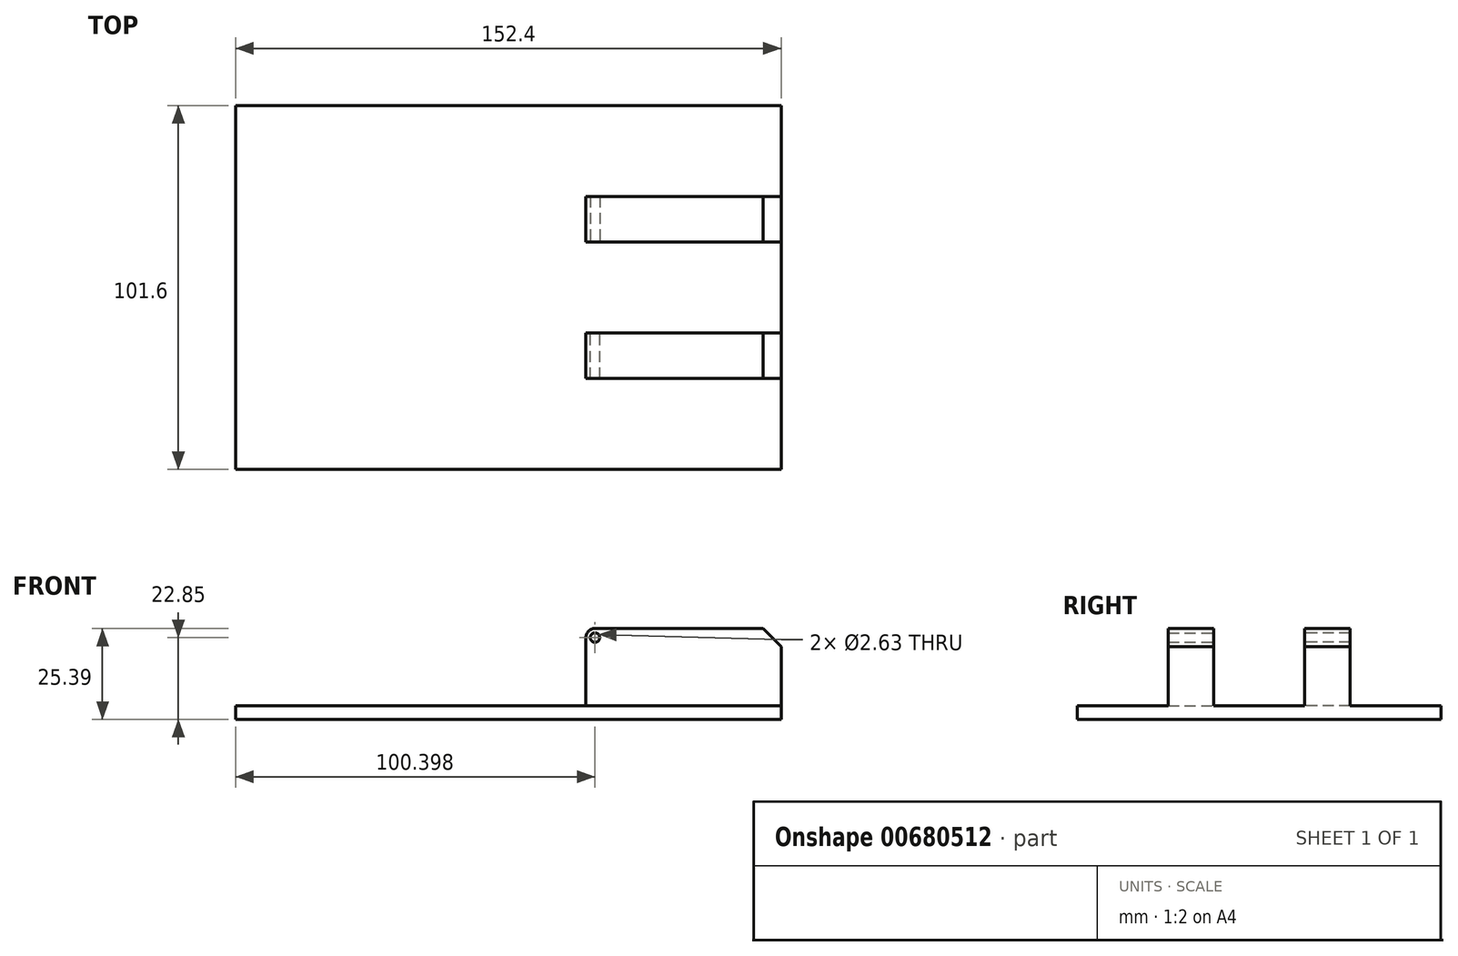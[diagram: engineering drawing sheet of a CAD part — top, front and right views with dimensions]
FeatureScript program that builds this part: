
annotation { "Feature Type Name" : "Feature", "Feature Type Description" : "" }
export const myFeature = defineFeature(function(context is Context, id is Id, definition is map)
    precondition{}
    {
        {
            var Q0;
            Q0=qCreatedBy(makeId("Front.planeOp"),FACE);
            var sketch = newSketch(context, id + "F0", { "sketchPlane" : qUnion([Q0])});
            skLineSegment(sketch, "E0.bottom", {"start": v(-7.2, 5.5) * mm, "end": v(145.2, 5.5) * mm});
            skLineSegment(sketch, "E0.top", {"start": v(-7.2, 1.7) * mm, "end": v(145.2, 1.7) * mm});
            skLineSegment(sketch, "E0.left", {"start": v(-7.2, 5.5) * mm, "end": v(-7.2, 1.7) * mm});
            skLineSegment(sketch, "E0.right", {"start": v(145.2, 5.5) * mm, "end": v(145.2, 1.7) * mm});
            skLineSegment(sketch, "E1.bottom", {"start": v(145.2, 5.5) * mm, "end": v(90.66, 5.5) * mm});
            skLineSegment(sketch, "E1.top", {"start": v(145.2, 27.08) * mm, "end": v(93.2, 27.08) * mm});
            skLineSegment(sketch, "E1.left", {"start": v(145.2, 5.5) * mm, "end": v(145.2, 27.08) * mm});
            skLineSegment(sketch, "E1.right", {"start": v(90.66, 5.5) * mm, "end": v(90.66, 24.54) * mm});
            skPoint(sketch, "E2.visualSharp", {"position": v(90.66, 27.08) * mm});
            skArc(sketch, "E2.filletArc", {"start": v(93.2, 27.08) * mm, "mid": v(91.4, 26.34) * mm, "end": v(90.66, 24.54) * mm});
            skCircle(sketch, "E3", {"center": v(93.2, 24.54) * mm, "radius": 1.31 * mm});
            skSolve(sketch);
        }
        {
            var Q0;
            Q0=makeQuery(id+"F0.imprint","IMPRINT",FACE,{"disambiguationData":[TD([[makeQuery(id+"F0.imprint","IMPRINT",EDGE,{"derivedFrom":sQuery(id+"F0.wireOp",EDGE,"E0.bottom")}),-1.0]])]});
            extrude(context, id + "F1", {"entities" : qUnion([Q0]), "endBound" : BoundingType.SYMMETRIC, "depth" : 101.6 * mm, "offsetDistance" : 25.4 * mm});
        }
        {
            var Q0;
            Q0 = qSketchRegion(id + "F0", true);
            extrude(context, id + "F2", {"entities" : qUnion([Q0]), "operationType" : NewBodyOperationType.ADD, "oppositeDirection" : true, "depth" : 25.4 * mm, "offsetDistance" : 25.4 * mm, "hasSecondDirection" : true, "secondDirectionOppositeDirection" : true, "secondDirectionDepth" : 12.7 * mm});
        }
        {
            var Q0;
            Q0 = qSketchRegion(id + "F0", true);
            extrude(context, id + "F3", {"entities" : qUnion([Q0]), "operationType" : NewBodyOperationType.ADD, "depth" : 25.4 * mm, "offsetDistance" : 25.4 * mm, "hasSecondDirection" : true, "secondDirectionOppositeDirection" : false, "secondDirectionDepth" : 12.7 * mm});
        }
        {
            var Q0;
            Q0=makeQuery(id+"F2.opExtrude","SWEPT_EDGE",EDGE,{"disambiguationData":[OSD([sQuery(id+"F0.wireOp",EDGE,"E1.top"),sQuery(id+"F0.wireOp",EDGE,"E1.left")])]});
            var Q1;
            Q1=makeQuery(id+"F3.opExtrude","SWEPT_EDGE",EDGE,{"disambiguationData":[OSD([sQuery(id+"F0.wireOp",EDGE,"E1.top"),sQuery(id+"F0.wireOp",EDGE,"E1.left")])]});
            chamfer(context, id + "F4", {"entities" : qUnion([Q0, Q1]), "width" : 5.08 * mm, "tangentPropagation" : true});
        }
    });
